# Revit family: HUNTER_FLOW-CLIK Interface Module
name_source: partatom
category: Electrical Fixtures
revit_build: Autodesk Revit 2017 (Build: 20190508_0315(x64)
units: mm (PartAtom-declared; Revit-internal decimal feet)

## family parameters
Cut with Voids When Loaded = No
Host = Face
Maintain Annotation Orientation = No
OmniClass Number = 23.27.11.11.23
Part Type = Normal
Room Calculation Point = No
Round Connector Dimension = Use Diameter
Shared = Yes

## types (1)
- WR-CLIK-R
    Assembly Code = G4030100
    Current = 0 A
    Default Elevation = 1219 mm
    Description = FLOW-CLIK® Flow-Sensor Interface Panel
    Distance Coverage = 300000 mm  [stored 984.252 ft]
    FLOW-CLIK Module = Flow- Clik Interface Panel
    Input Voltage = 24 V
    Keynote = 32 84 23.05
    Manufacturer = Hunter® Industries
    Model = FLOW-CLIK®
    Panel Coverage Zone = Yes
    Panel Symbol = Yes
    Panel height = 83 mm  [stored 0.27231 ft]
    Panel length = 100 mm  [stored 0.328084 ft]
    Power = 1 VA
    Rain-Clik = 0 mm  [stored 0 ft]
    Type Comments = FLOW-CLIK® Interface Panel
    URL = https://www.hunterindustries.com

note: [stored X ft] marks values corroborated as IEEE doubles in the binary element streams (Revit-internal decimal feet)

## geometry (parser evidence)
native form markers: Sweep x5
no freeform markers — native parametric forms only
